# Revit family: Spirit Caño Alto
name_source: partatom
category: Plumbing Fixtures
revit_build: Autodesk Revit 2017 (Build: 20160225_1515(x64)
units: mm (PartAtom-declared; Revit-internal decimal feet)

## family parameters
Always vertical = Yes
Cut with Voids When Loaded = No
OmniClass Number = 23.45.00.00
OmniClass Title = Sanitary, Laundry, and Cleaning Equipment
Part Type = Normal
Room Calculation Point = No
Round Connector Dimension = Use Diameter
Shared = No
Work Plane-Based = No

## types (1)
- Spirit Caño Alto
    Acabado Grifo = Teka_Niquel Cromo
    Ca_1_Aireador anticalcáreo cromado = Yes
    Ca_1_Cartucho de disco cerámico de elevada resistencia = Yes
    Ca_1_Garantía = 5 años
    Ca_1_Incluye flexibles homologados. = Yes
    Ca_1_Modelo para Baño-Ducha = No
    Ca_1_Modelo para Lavamanos = No
    Ca_1_Modelo para ducha = Yes
    Ca_1_Modelo para ducha empotrada = No
    Ca_1_Modelo para lavamanos tipo vanitorio = Yes
    Ca_1_Sistema regulador de caudal y temperatura = Yes
    Ca_1_Superficie cromada de aprox. = 12,5 micras Niquel-Cromo
    Ca_Alto = 362 mm  [stored 1.18766 ft]
    Ca_Ancho = 104 mm
    Ca_Certificaciones = Norma UNE
    Ca_Creado por = Catálogo Arquitectura
    Ca_Código Catálogo Arquitectura = 412_Tek_074
    Ca_Código EAN = 8413509205838
    Ca_Código del Producto = 553110210
    Ca_Especificaciones Técnicas = Monomando caño alto sobre cubierta para vanitorio modelo Spirit Caño Alto
    Ca_Fabricante = Teka
    Ca_Instalación = Sobre cubierta
    Ca_Itemizado CDT = E 04 00 00
    Ca_Masterformat = 22 41 39
    Ca_Material Principal = Latón con acabado en Niquel Cromo
    Ca_País de Fabricación = China (Planta TEKA)
    Ca_Producto = Spirit Caño Alto
    Ca_Representante = Teka
    Ca_Teléfono = 99821 1017
    Ca_Usos = Monomando caño alto para vanitorio
    Ca_Web del Fabricante = www.teka.cl
    Ca_Web del Representante = www.teka.cl
    Description = Monomando caño alto para vanitorio
    Logo Teka = <By Category>
    Manufacturer = Teka
    Model = Spirit Caño Alto
    URL = www.teka.cl

note: [stored X ft] marks values corroborated as IEEE doubles in the binary element streams (Revit-internal decimal feet)

## geometry (parser evidence)
native form markers: Sweep x3
no freeform markers — native parametric forms only
